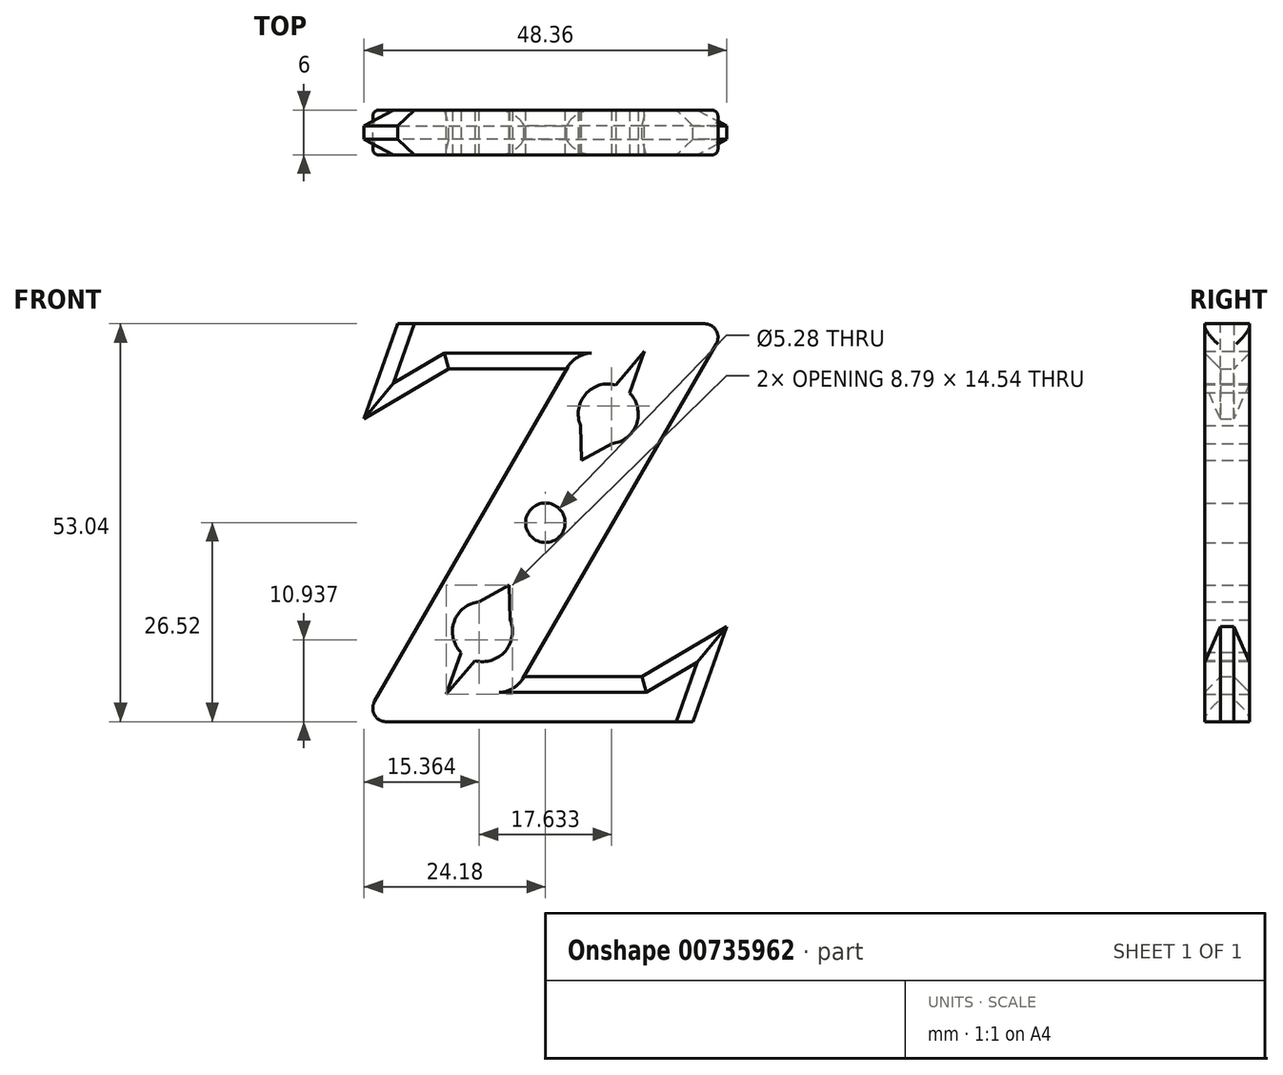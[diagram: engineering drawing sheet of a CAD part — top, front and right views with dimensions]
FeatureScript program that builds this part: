
annotation { "Feature Type Name" : "Feature", "Feature Type Description" : "" }
export const myFeature = defineFeature(function(context is Context, id is Id, definition is map)
    precondition{}
    {
        {
            var Q0;
            Q0=qCreatedBy(makeId("Front.planeOp"),FACE);
            var sketch = newSketch(context, id + "F0", { "sketchPlane" : qUnion([Q0])});
            skCircle(sketch, "E0", {"center": v(0, 0) * mm, "radius": 4 * mm, "construction": true});
            skCircle(sketch, "E1", {"center": v(0, 0) * mm, "radius": 11 * mm});
            skCircle(sketch, "E2", {"center": v(0, 0) * mm, "radius": 13 * mm});
            skLineSegment(sketch, "E3", {"start": v(10.54, 44.2) * mm, "end": v(-40.57, -44.2) * mm});
            skLineSegment(sketch, "E4", {"start": v(40.57, 44.2) * mm, "end": v(-10.54, -44.2) * mm});
            skLineSegment(sketch, "E5", {"start": v(10.54, 44.2) * mm, "end": v(40.57, 44.2) * mm});
            skLineSegment(sketch, "E6", {"start": v(-40.57, -44.2) * mm, "end": v(-10.54, -44.2) * mm});
            skLineSegment(sketch, "E7", {"start": v(8, 13.85) * mm, "end": v(7.85, 21.57) * mm});
            skPoint(sketch, "E8", {"position": v(22.02, 38.1) * mm});
            skLineSegment(sketch, "E9", {"start": v(8, 13.85) * mm, "end": v(14.77, 17.56) * mm});
            skLineSegment(sketch, "E10", {"start": v(7.85, 21.57) * mm, "end": v(22.02, 38.1) * mm});
            skLineSegment(sketch, "E11", {"start": v(14.77, 17.56) * mm, "end": v(22.02, 38.1) * mm});
            skLineSegment(sketch, "E12.1.0", {"start": v(-8, -13.85) * mm, "end": v(-7.85, -21.57) * mm});
            skLineSegment(sketch, "E12.1.1", {"start": v(-8, -13.85) * mm, "end": v(-14.77, -17.56) * mm});
            skLineSegment(sketch, "E12.1.2", {"start": v(-14.77, -17.56) * mm, "end": v(-22.02, -38.1) * mm});
            skLineSegment(sketch, "E12.1.3", {"start": v(-7.85, -21.57) * mm, "end": v(-22.02, -38.1) * mm});
            skLineSegment(sketch, "E13", {"start": v(10.54, 44.2) * mm, "end": v(-32.8, 44.2) * mm});
            skLineSegment(sketch, "E14", {"start": v(-32.8, 44.2) * mm, "end": v(-40.3, 23.07) * mm});
            skLineSegment(sketch, "E15", {"start": v(-40.3, 23.07) * mm, "end": v(-21.46, 34.2) * mm});
            skLineSegment(sketch, "E16", {"start": v(-21.46, 34.2) * mm, "end": v(4.76, 34.2) * mm});
            skLineSegment(sketch, "E17.1.0", {"start": v(-10.54, -44.2) * mm, "end": v(32.8, -44.2) * mm});
            skLineSegment(sketch, "E17.1.1", {"start": v(21.46, -34.2) * mm, "end": v(-4.76, -34.2) * mm});
            skLineSegment(sketch, "E17.1.2", {"start": v(40.3, -23.07) * mm, "end": v(21.46, -34.2) * mm});
            skLineSegment(sketch, "E17.1.3", {"start": v(32.8, -44.2) * mm, "end": v(40.3, -23.07) * mm});
            skCircle(sketch, "E18", {"center": v(30.63, 38.72) * mm, "radius": 5 * mm});
            skCircle(sketch, "E19", {"center": v(30.63, 38.72) * mm, "radius": 4 * mm});
            skCircle(sketch, "E20", {"center": v(-28.36, 38.08) * mm, "radius": 5 * mm});
            skCircle(sketch, "E21", {"center": v(-28.36, 38.08) * mm, "radius": 4 * mm});
            skCircle(sketch, "E22.1.0", {"center": v(-30.7, -38.63) * mm, "radius": 5 * mm});
            skCircle(sketch, "E22.1.1", {"center": v(-30.7, -38.63) * mm, "radius": 4 * mm});
            skCircle(sketch, "E22.1.2", {"center": v(28.27, -37.99) * mm, "radius": 5 * mm});
            skCircle(sketch, "E22.1.3", {"center": v(28.27, -37.99) * mm, "radius": 4 * mm});
            skPoint(sketch, "E22.center", {"position": v(-0.04, 0.05) * mm});
            skCircle(sketch, "E23", {"center": v(0, 0) * mm, "radius": 4.4 * mm});
            skSolve(sketch);
        }
        {
            var Q0;
            {var subQ0=sQuery(id+"F0.wireOp",EDGE,"E6");Q0=makeQuery(id+"F0.imprint","IMPRINT",FACE,{"disambiguationData":[TD([[makeQuery(id+"F0.imprint","IMPRINT",EDGE,{"derivedFrom":subQ0}),1.0]])]});}
            var Q1;
            Q1=makeQuery(id+"F0.imprint","IMPRINT",FACE,{"disambiguationData":[TD([[makeQuery(id+"F0.imprint","IMPRINT",EDGE,{"derivedFrom":sQuery(id+"F0.wireOp",EDGE,"E1")}),-1.0]])]});
            var Q2;
            Q2=makeQuery(id+"F0.imprint","IMPRINT",FACE,{"disambiguationData":[TD([[makeQuery(id+"F0.imprint","IMPRINT",EDGE,{"derivedFrom":sQuery(id+"F0.wireOp",EDGE,"E7")}),1.0]])]});
            var Q3;
            {var subQ1=sQuery(id+"F0.wireOp",EDGE,"E17.1.0");Q3=makeQuery(id+"F0.imprint","IMPRINT",FACE,{"disambiguationData":[TD([[makeQuery(id+"F0.imprint","IMPRINT",EDGE,{"derivedFrom":subQ1}),1.0]])]});}
            var Q4;
            Q4=makeQuery(id+"F0.imprint","IMPRINT",FACE,{"disambiguationData":[TD([[makeQuery(id+"F0.imprint","IMPRINT",EDGE,{"derivedFrom":sQuery(id+"F0.wireOp",EDGE,"E22.1.1")}),-1.0]])]});
            var Q5;
            Q5=makeQuery(id+"F0.imprint","IMPRINT",FACE,{"disambiguationData":[TD([[makeQuery(id+"F0.imprint","IMPRINT",EDGE,{"derivedFrom":sQuery(id+"F0.wireOp",EDGE,"E22.1.2")}),1.0]])]});
            var Q6;
            {var subQ0=sQuery(id+"F0.wireOp",EDGE,"E5");var subQ1=sQuery(id+"F0.wireOp",EDGE,"E4");var subQ2=makeQuery(id+"F0.imprint","INTERSECT",VERTEX,{"derivedFrom":[subQ1,subQ0]});Q6=makeQuery(id+"F0.imprint","IMPRINT",FACE,{"disambiguationData":[TD([[makeQuery(id+"F0.imprint","IMPRINT",EDGE,{"disambiguationData":[TD([[subQ2,-1.0]])],"derivedFrom":subQ1}),-1.0]])]});}
            var Q7;
            Q7=makeQuery(id+"F0.imprint","IMPRINT",FACE,{"disambiguationData":[TD([[makeQuery(id+"F0.imprint","IMPRINT",EDGE,{"derivedFrom":sQuery(id+"F0.wireOp",EDGE,"E19")}),-1.0]])]});
            var Q8;
            {var subQ0=sQuery(id+"F0.wireOp",EDGE,"E15");Q8=makeQuery(id+"F0.imprint","IMPRINT",FACE,{"disambiguationData":[TD([[makeQuery(id+"F0.imprint","IMPRINT",EDGE,{"derivedFrom":subQ0}),1.0]])]});}
            var Q9;
            Q9=makeQuery(id+"F0.imprint","IMPRINT",FACE,{"disambiguationData":[TD([[makeQuery(id+"F0.imprint","IMPRINT",EDGE,{"derivedFrom":sQuery(id+"F0.wireOp",EDGE,"E21")}),-1.0]])]});
            var Q10;
            {var subQ0=sQuery(id+"F0.wireOp",EDGE,"E14");var subQ1=sQuery(id+"F0.wireOp",EDGE,"E13");var subQ2=makeQuery(id+"F0.imprint","INTERSECT",VERTEX,{"derivedFrom":[subQ1,subQ0]});Q10=makeQuery(id+"F0.imprint","IMPRINT",FACE,{"disambiguationData":[TD([[makeQuery(id+"F0.imprint","IMPRINT",EDGE,{"disambiguationData":[TD([[subQ2,1.0]])],"derivedFrom":subQ1}),1.0]])]});}
            var Q11;
            Q11=makeQuery(id+"F0.imprint","IMPRINT",FACE,{"disambiguationData":[TD([[makeQuery(id+"F0.imprint","IMPRINT",EDGE,{"derivedFrom":sQuery(id+"F0.wireOp",EDGE,"E21")}),1.0]])]});
            var Q12;
            Q12=makeQuery(id+"F0.imprint","IMPRINT",FACE,{"disambiguationData":[TD([[makeQuery(id+"F0.imprint","IMPRINT",EDGE,{"derivedFrom":sQuery(id+"F0.wireOp",EDGE,"E19")}),1.0]])]});
            var Q13;
            Q13=makeQuery(id+"F0.imprint","IMPRINT",FACE,{"disambiguationData":[TD([[makeQuery(id+"F0.imprint","IMPRINT",EDGE,{"derivedFrom":sQuery(id+"F0.wireOp",EDGE,"E22.1.1")}),1.0]])]});
            var Q14;
            Q14=makeQuery(id+"F0.imprint","IMPRINT",FACE,{"disambiguationData":[TD([[makeQuery(id+"F0.imprint","IMPRINT",EDGE,{"derivedFrom":sQuery(id+"F0.wireOp",EDGE,"E22.1.3")}),1.0]])]});
            var Q15;
            Q15=makeQuery(id+"F0.imprint","IMPRINT",FACE,{"disambiguationData":[TD([[makeQuery(id+"F0.imprint","IMPRINT",EDGE,{"derivedFrom":sQuery(id+"F0.wireOp",EDGE,"E1")}),1.0]])]});
            extrude(context, id + "F1", {"entities" : qUnion([Q0, Q1, Q2, Q3, Q4, Q5, Q6, Q7, Q8, Q9, Q10, Q11, Q12, Q13, Q14, Q15]), "depth" : 10 * mm, "offsetDistance" : 25 * mm});
        }
        {
            var Q0;
            Q0=makeQuery(id+"F1.opExtrude","CAP_EDGE",EDGE,{"disambiguationData":[OSD([sQuery(id+"F0.wireOp",EDGE,"E4")])],"isStart":false});
            var Q1;
            Q1=makeQuery(id+"F1.opExtrude","CAP_EDGE",EDGE,{"disambiguationData":[OSD([sQuery(id+"F0.wireOp",EDGE,"E4")])],"isStart":true});
            var Q2;
            Q2=makeQuery(id+"F1.opExtrude","CAP_EDGE",EDGE,{"disambiguationData":[OSD([sQuery(id+"F0.wireOp",EDGE,"E3")])],"isStart":false});
            var Q3;
            Q3=makeQuery(id+"F1.opExtrude","CAP_EDGE",EDGE,{"disambiguationData":[OSD([sQuery(id+"F0.wireOp",EDGE,"E3")])],"isStart":true});
            var Q4;
            Q4=makeQuery(id+"F1.opExtrude","SWEPT_EDGE",EDGE,{"disambiguationData":[OSD([sQuery(id+"F0.wireOp",EDGE,"E3"),sQuery(id+"F0.wireOp",EDGE,"E6")])]});
            var Q5;
            Q5=makeQuery(id+"F1.opExtrude","SWEPT_EDGE",EDGE,{"disambiguationData":[OSD([sQuery(id+"F0.wireOp",EDGE,"E4"),sQuery(id+"F0.wireOp",EDGE,"E5")])]});
            fillet(context, id + "F2", {"entities" : qUnion([Q0, Q1, Q2, Q3, Q4, Q5]), "radius" : 3 * mm, "tangentPropagation" : true, "allowEdgeOverflow" : false});
        }
        {
            var Q0;
            Q0=makeQuery(id+"F1.opExtrude","CAP_EDGE",EDGE,{"disambiguationData":[OSD([sQuery(id+"F0.wireOp",EDGE,"E16")])],"isStart":false});
            var Q1;
            Q1=makeQuery(id+"F1.opExtrude","CAP_EDGE",EDGE,{"disambiguationData":[OSD([sQuery(id+"F0.wireOp",EDGE,"E15")])],"isStart":false});
            var Q2;
            Q2=makeQuery(id+"F1.opExtrude","CAP_EDGE",EDGE,{"disambiguationData":[OSD([sQuery(id+"F0.wireOp",EDGE,"E14")])],"isStart":false});
            var Q3;
            Q3=makeQuery(id+"F1.opExtrude","CAP_EDGE",EDGE,{"disambiguationData":[OSD([sQuery(id+"F0.wireOp",EDGE,"E14")])],"isStart":true});
            var Q4;
            Q4=makeQuery(id+"F1.opExtrude","CAP_EDGE",EDGE,{"disambiguationData":[OSD([sQuery(id+"F0.wireOp",EDGE,"E16")])],"isStart":true});
            var Q5;
            Q5=makeQuery(id+"F1.opExtrude","CAP_EDGE",EDGE,{"disambiguationData":[OSD([sQuery(id+"F0.wireOp",EDGE,"E15")])],"isStart":true});
            var Q6;
            Q6=makeQuery(id+"F1.opExtrude","CAP_EDGE",EDGE,{"disambiguationData":[OSD([sQuery(id+"F0.wireOp",EDGE,"E17.1.1")])],"isStart":false});
            var Q7;
            Q7=makeQuery(id+"F1.opExtrude","CAP_EDGE",EDGE,{"disambiguationData":[OSD([sQuery(id+"F0.wireOp",EDGE,"E17.1.1")])],"isStart":true});
            var Q8;
            Q8=makeQuery(id+"F1.opExtrude","CAP_EDGE",EDGE,{"disambiguationData":[OSD([sQuery(id+"F0.wireOp",EDGE,"E17.1.2")])],"isStart":true});
            var Q9;
            Q9=makeQuery(id+"F1.opExtrude","CAP_EDGE",EDGE,{"disambiguationData":[OSD([sQuery(id+"F0.wireOp",EDGE,"E17.1.2")])],"isStart":false});
            var Q10;
            Q10=makeQuery(id+"F1.opExtrude","CAP_EDGE",EDGE,{"disambiguationData":[OSD([sQuery(id+"F0.wireOp",EDGE,"E17.1.3")])],"isStart":false});
            var Q11;
            Q11=makeQuery(id+"F1.opExtrude","CAP_EDGE",EDGE,{"disambiguationData":[OSD([sQuery(id+"F0.wireOp",EDGE,"E17.1.3")])],"isStart":true});
            chamfer(context, id + "F3", {"entities" : qUnion([Q0, Q1, Q2, Q3, Q4, Q5, Q6, Q7, Q8, Q9, Q10, Q11]), "width" : 3.5 * mm, "tangentPropagation" : true});
        }
        {
            var Q0;
            Q0=makeQuery(id+"F1.opExtrude","SWEPT_BODY",BODY,{"disambiguationData":[OSD([sQuery(id+"F0.wireOp",EDGE,"E1"),sQuery(id+"F0.wireOp",EDGE,"E3"),sQuery(id+"F0.wireOp",EDGE,"E4"),sQuery(id+"F0.wireOp",EDGE,"E5"),sQuery(id+"F0.wireOp",EDGE,"E6"),sQuery(id+"F0.wireOp",EDGE,"E7"),sQuery(id+"F0.wireOp",EDGE,"E9"),sQuery(id+"F0.wireOp",EDGE,"E10"),sQuery(id+"F0.wireOp",EDGE,"E11"),sQuery(id+"F0.wireOp",EDGE,"E12.1.0"),sQuery(id+"F0.wireOp",EDGE,"E12.1.1"),sQuery(id+"F0.wireOp",EDGE,"E12.1.2"),sQuery(id+"F0.wireOp",EDGE,"E12.1.3"),sQuery(id+"F0.wireOp",EDGE,"E13"),sQuery(id+"F0.wireOp",EDGE,"E14"),sQuery(id+"F0.wireOp",EDGE,"E15"),sQuery(id+"F0.wireOp",EDGE,"E16"),sQuery(id+"F0.wireOp",EDGE,"E17.1.0"),sQuery(id+"F0.wireOp",EDGE,"E17.1.1"),sQuery(id+"F0.wireOp",EDGE,"E17.1.2"),sQuery(id+"F0.wireOp",EDGE,"E17.1.3"),sQuery(id+"F0.wireOp",EDGE,"E19"),sQuery(id+"F0.wireOp",EDGE,"E21"),sQuery(id+"F0.wireOp",EDGE,"E22.1.1"),sQuery(id+"F0.wireOp",EDGE,"E22.1.3")])]});
            var Q1;
            Q1=qCreatedBy(makeId("Origin.pointOp"),VERTEX);
            transform(context, id + "F4", {"entities" : qUnion([Q0]), "transformType" : TransformType.SCALE_UNIFORMLY, "scale" : .6, "scalePoint" : qUnion([Q1]), "makeCopy" : false});
        }
        {
            var Q0;
            Q0=makeQuery(id+"F1.opExtrude","CAP_FACE",FACE,{"disambiguationData":[OSD([sQuery(id+"F0.wireOp",EDGE,"E3"),sQuery(id+"F0.wireOp",EDGE,"E4"),sQuery(id+"F0.wireOp",EDGE,"E5"),sQuery(id+"F0.wireOp",EDGE,"E6"),sQuery(id+"F0.wireOp",EDGE,"E7"),sQuery(id+"F0.wireOp",EDGE,"E9"),sQuery(id+"F0.wireOp",EDGE,"E10"),sQuery(id+"F0.wireOp",EDGE,"E11"),sQuery(id+"F0.wireOp",EDGE,"E12.1.0"),sQuery(id+"F0.wireOp",EDGE,"E12.1.1"),sQuery(id+"F0.wireOp",EDGE,"E12.1.2"),sQuery(id+"F0.wireOp",EDGE,"E12.1.3"),sQuery(id+"F0.wireOp",EDGE,"E13"),sQuery(id+"F0.wireOp",EDGE,"E14"),sQuery(id+"F0.wireOp",EDGE,"E15"),sQuery(id+"F0.wireOp",EDGE,"E16"),sQuery(id+"F0.wireOp",EDGE,"E17.1.0"),sQuery(id+"F0.wireOp",EDGE,"E17.1.1"),sQuery(id+"F0.wireOp",EDGE,"E17.1.2"),sQuery(id+"F0.wireOp",EDGE,"E17.1.3"),sQuery(id+"F0.wireOp",EDGE,"E23")])],"isStart":false});
            var sketch = newSketch(context, id + "F5", { "sketchPlane" : qUnion([Q0])});
            skCircle(sketch, "E24", {"center": v(8.39, 14.5) * mm, "radius": 4 * mm});
            skPoint(sketch, "E24.first.point", {"position": v(4.7, 12.94) * mm});
            skPoint(sketch, "E24.second.point", {"position": v(8.86, 10.54) * mm});
            skPoint(sketch, "E24.third.point", {"position": v(10.35, 18) * mm});
            skCircle(sketch, "E25.1.0", {"center": v(-8.39, -14.5) * mm, "radius": 4 * mm});
            skPoint(sketch, "E25.center", {"position": v(0, 0) * mm});
            skSolve(sketch);
        }
        {
            var Q0;
            {var subQ0=sQuery(id+"F5.wireOp",EDGE,"E24");var subQ1=makeQuery(id+"F1.opExtrude","CAP_EDGE",EDGE,{"disambiguationData":[OSD([sQuery(id+"F0.wireOp",EDGE,"E10")])],"isStart":false});var subQ3=makeQuery(id+"F5.imprint","INTERSECT",VERTEX,{"derivedFrom":[subQ1,subQ0]});Q0=makeQuery(id+"F5.imprint","IMPRINT",FACE,{"disambiguationData":[TD([[makeQuery(id+"F5.imprint","IMPRINT",EDGE,{"disambiguationData":[TD([[subQ3,-1.0]])],"derivedFrom":subQ0}),1.0]])]});}
            var Q1;
            {var subQ0=sQuery(id+"F5.wireOp",EDGE,"E24");var subQ1=makeQuery(id+"F1.opExtrude","CAP_EDGE",EDGE,{"disambiguationData":[OSD([sQuery(id+"F0.wireOp",EDGE,"E11")])],"isStart":false});var subQ3=makeQuery(id+"F5.imprint","INTERSECT",VERTEX,{"derivedFrom":[subQ1,subQ0]});Q1=makeQuery(id+"F5.imprint","IMPRINT",FACE,{"disambiguationData":[TD([[makeQuery(id+"F5.imprint","IMPRINT",EDGE,{"disambiguationData":[TD([[subQ3,1.0]])],"derivedFrom":subQ0}),1.0]])]});}
            var Q2;
            {var subQ0=sQuery(id+"F5.wireOp",EDGE,"E25.1.0");var subQ1=makeQuery(id+"F1.opExtrude","CAP_EDGE",EDGE,{"disambiguationData":[OSD([sQuery(id+"F0.wireOp",EDGE,"E12.1.2")])],"isStart":false});var subQ3=makeQuery(id+"F5.imprint","INTERSECT",VERTEX,{"derivedFrom":[subQ1,subQ0]});Q2=makeQuery(id+"F5.imprint","IMPRINT",FACE,{"disambiguationData":[TD([[makeQuery(id+"F5.imprint","IMPRINT",EDGE,{"disambiguationData":[TD([[subQ3,1.0]])],"derivedFrom":subQ0}),1.0]])]});}
            var Q3;
            {var subQ0=sQuery(id+"F5.wireOp",EDGE,"E25.1.0");var subQ1=makeQuery(id+"F1.opExtrude","CAP_EDGE",EDGE,{"disambiguationData":[OSD([sQuery(id+"F0.wireOp",EDGE,"E12.1.3")])],"isStart":false});var subQ3=makeQuery(id+"F5.imprint","INTERSECT",VERTEX,{"derivedFrom":[subQ1,subQ0]});Q3=makeQuery(id+"F5.imprint","IMPRINT",FACE,{"disambiguationData":[TD([[makeQuery(id+"F5.imprint","IMPRINT",EDGE,{"disambiguationData":[TD([[subQ3,-1.0]])],"derivedFrom":subQ0}),1.0]])]});}
            extrude(context, id + "F6", {"entities" : qUnion([Q0, Q1, Q2, Q3]), "operationType" : NewBodyOperationType.REMOVE, "oppositeDirection" : true, "depth" : 25 * mm, "offsetDistance" : 25 * mm});
        }
    });
